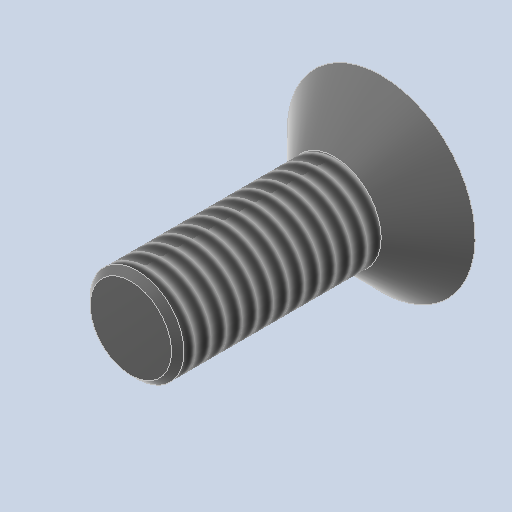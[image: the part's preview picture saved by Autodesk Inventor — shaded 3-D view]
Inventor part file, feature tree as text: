
AUTODESK INVENTOR PART (.ipt)
format: ipt  version: 2022 (Build 260153000, 153)  size: 173,056 bytes
history: native  units: in
note: dims shown in document units (in); Inventor stores cm internally (conversion verified against a paired STEP export)
features: sketch x2, revolve x1, extrude x1, chamfer x1, thread x1
ambient origin geometry x8: Origin, YZ Plane, XZ Plane, XY Plane, X Axis, Y Axis, Z Axis, Center Point
bodies: Body1 (feature_tree)
feature tree (6):
  revolve  "Revolution1"  [1 undecoded]
  extrude  "Extrusion5"  TaperAngle=45.0deg  [1 undecoded]
  chamfer  "Chamfer2"  Angle=90.0deg  [1 undecoded]
  thread  "Thread1"  [1 undecoded]
  sketch  "Sketch4"  dims[d11=0.2362in d12=0.1181in]
  sketch  "Sketch5"  dims[d15=0.315in d16=45.0deg d17=90.0deg d18=0.0787in d19=0.0472in d20=0.0in d21=0.0079in d22=0.0787in d23=45.0deg d24=0.1693in d25=0.0in]
note: 4 required parameter values undecoded (feature->parameter linkage not recoverable at this tier; creation-order binding heuristic only, values carry confidence <= 0.55)